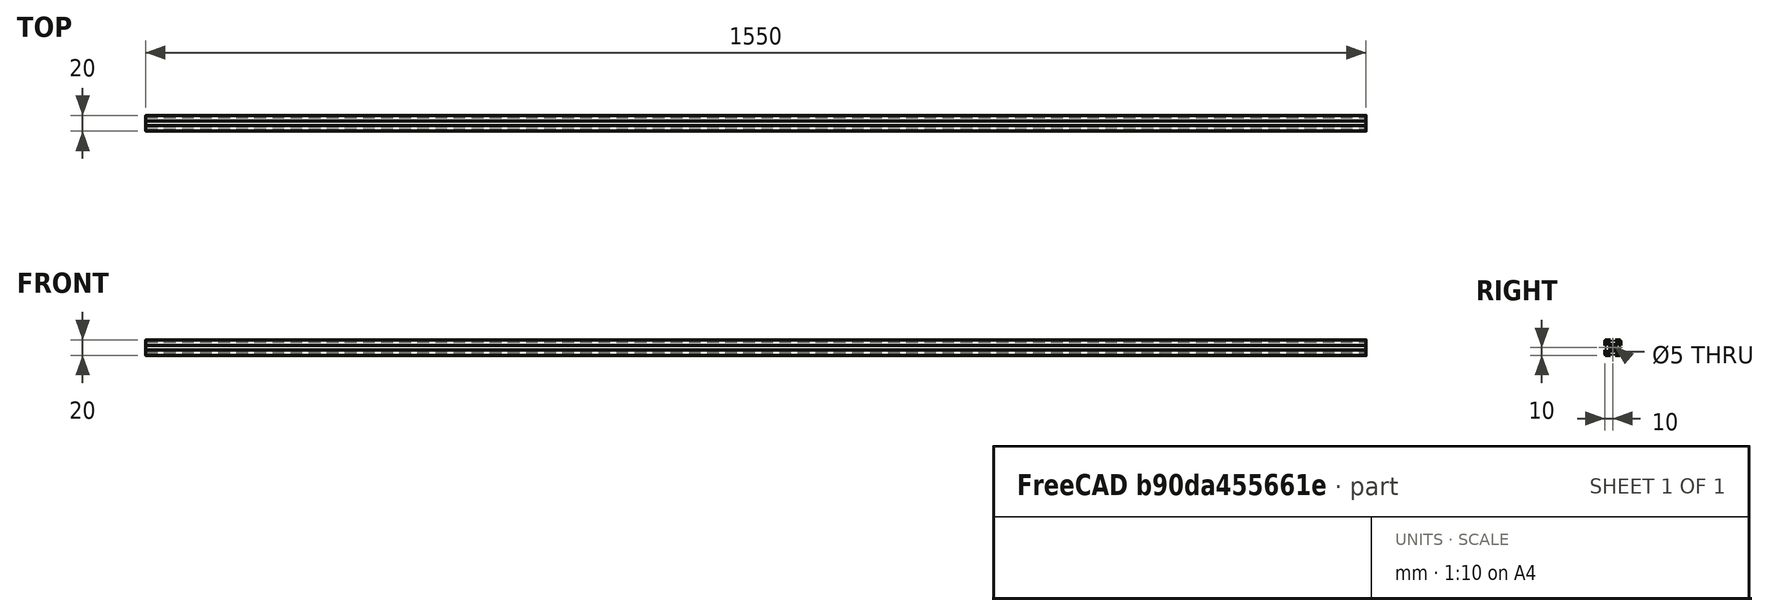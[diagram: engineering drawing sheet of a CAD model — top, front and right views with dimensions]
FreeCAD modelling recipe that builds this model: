
FCSTD DOCUMENT  (FreeCAD 0.19R24267 +99 (Git))
Label: 2020 Rail strut main long section 1550mm
License: All rights reserved
LicenseURL: http://en.wikipedia.org/wiki/All_rights_reserved
objects: Sketcher::SketchObject×1, PartDesign::Pad×1, PartDesign::Body×1
note: 4 computed .brp shape members not serialized (recipe doc carries the construction recipe); baked Part::Feature solids carry a one-line shape summary decoded from their .brp

FEATURE [Sketcher::SketchObject] Sketch  label="Rail cross section"
  FullyConstrained = true
  MapMode = 5
  Placement = pos=(0,0,0) rot=(0.57735,0.57735,0.57735;2.0944rad)
  Support = -> [YZ_Plane]
  sketch-geometry (47):
    g0: ArcOfCircle CenterX=-8 CenterY=8 CenterZ=0 NormalX=0 NormalY=0 NormalZ=1 AngleXU=0 Radius=2 StartAngle=1.5708 EndAngle=3.14159
    g1: ArcOfCircle CenterX=-8 CenterY=-8 CenterZ=0 NormalX=0 NormalY=0 NormalZ=1 AngleXU=0 Radius=2 StartAngle=3.14159 EndAngle=4.71239
    g2: ArcOfCircle CenterX=8 CenterY=-8 CenterZ=0 NormalX=0 NormalY=0 NormalZ=1 AngleXU=0 Radius=2 StartAngle=4.71239 EndAngle=6.28319
    g3: ArcOfCircle CenterX=8 CenterY=8 CenterZ=0 NormalX=0 NormalY=0 NormalZ=1 AngleXU=0 Radius=2 StartAngle=1e-16 EndAngle=1.5708
    g4: Circle CenterX=0 CenterY=0 CenterZ=0 NormalX=0 NormalY=0 NormalZ=1 AngleXU=0 Radius=2.5
    g5: LineSegment StartX=-10 StartY=8 StartZ=0 EndX=-10 EndY=3 EndZ=0
    g6: LineSegment StartX=-10 StartY=-3 StartZ=0 EndX=-10 EndY=-8 EndZ=0
    g7: LineSegment StartX=-8 StartY=-10 StartZ=0 EndX=-3 EndY=-10 EndZ=0
    g8: LineSegment StartX=3 StartY=-10 StartZ=0 EndX=8 EndY=-10 EndZ=0
    g9: LineSegment StartX=10 StartY=-8 StartZ=0 EndX=10 EndY=-3 EndZ=0
    g10: LineSegment StartX=10 StartY=3 StartZ=0 EndX=10 EndY=8 EndZ=0
    g11: LineSegment StartX=-8 StartY=10 StartZ=0 EndX=-3 EndY=10 EndZ=0
    g12: LineSegment StartX=3 StartY=10 StartZ=0 EndX=8 EndY=10 EndZ=0
    g13: LineSegment StartX=-3 StartY=4 StartZ=0 EndX=3 EndY=4 EndZ=0
    g14: LineSegment StartX=4 StartY=3 StartZ=0 EndX=4 EndY=-3 EndZ=0
    g15: LineSegment StartX=3 StartY=-4 StartZ=0 EndX=-3 EndY=-4 EndZ=0
    g16: LineSegment StartX=-4 StartY=-3 StartZ=0 EndX=-4 EndY=3 EndZ=0
    g17: LineSegment StartX=-3 StartY=-4 StartZ=0 EndX=-7 EndY=-8 EndZ=0
    g18: LineSegment StartX=-3 StartY=-10 StartZ=0 EndX=-3 EndY=-8 EndZ=0
    g19: LineSegment StartX=3 StartY=-4 StartZ=0 EndX=7 EndY=-8 EndZ=0
    g20: LineSegment StartX=4 StartY=-3 StartZ=0 EndX=8 EndY=-7 EndZ=0
    g21: LineSegment StartX=8 StartY=-7 StartZ=0 EndX=8 EndY=-3 EndZ=0
    g22: LineSegment StartX=10 StartY=-3 StartZ=0 EndX=8 EndY=-3 EndZ=0
    g23: LineSegment StartX=4 StartY=3 StartZ=0 EndX=8 EndY=7 EndZ=0
    g24: LineSegment StartX=8 StartY=7 StartZ=0 EndX=8 EndY=3 EndZ=0
    g25: LineSegment StartX=8 StartY=3 StartZ=0 EndX=10 EndY=3 EndZ=0
    g26: LineSegment StartX=3 StartY=10 StartZ=0 EndX=3 EndY=8 EndZ=0
    g27: LineSegment StartX=3 StartY=8 StartZ=0 EndX=7 EndY=8 EndZ=0
    g28: LineSegment StartX=7 StartY=8 StartZ=0 EndX=3 EndY=4 EndZ=0
    g29: LineSegment StartX=-3 StartY=4 StartZ=0 EndX=-7 EndY=8 EndZ=0
    g30: LineSegment StartX=-7 StartY=8 StartZ=0 EndX=-3 EndY=8 EndZ=0
    g31: LineSegment StartX=-3 StartY=8 StartZ=0 EndX=-3 EndY=10 EndZ=0
    g32: LineSegment StartX=-4 StartY=3 StartZ=0 EndX=-8 EndY=7 EndZ=0
    g33: LineSegment StartX=-8 StartY=3 StartZ=0 EndX=-10 EndY=3 EndZ=0
    g34: LineSegment StartX=-10 StartY=-3 StartZ=0 EndX=-8 EndY=-3 EndZ=0
    g35: LineSegment StartX=-8 StartY=-7 StartZ=0 EndX=-4 EndY=-3 EndZ=0
    g36: LineSegment StartX=3 StartY=-10 StartZ=0 EndX=3 EndY=-8 EndZ=0
    g37: LineSegment StartX=3 StartY=-8 StartZ=0 EndX=7 EndY=-8 EndZ=0
    g38: LineSegment StartX=-3 StartY=-8 StartZ=0 EndX=-7 EndY=-8 EndZ=0
    g39: LineSegment StartX=-8 StartY=-7 StartZ=0 EndX=-8 EndY=-3 EndZ=0
    g40: LineSegment StartX=-8 StartY=3 StartZ=0 EndX=-8 EndY=7 EndZ=0
    g41: LineSegment StartX=-3 StartY=10 StartZ=0 EndX=3 EndY=10 EndZ=0
    g42: LineSegment StartX=10 StartY=3 StartZ=0 EndX=10 EndY=-3 EndZ=0
    g43: LineSegment StartX=3 StartY=-10 StartZ=0 EndX=-3 EndY=-10 EndZ=0
    g44: LineSegment StartX=-10 StartY=-3 StartZ=0 EndX=-10 EndY=3 EndZ=0
    g45: LineSegment StartX=-4 StartY=-3 StartZ=0 EndX=-3 EndY=-4 EndZ=0
    g46: LineSegment StartX=-8 StartY=-7 StartZ=0 EndX=-7 EndY=-8 EndZ=0
  constraints (128):
    c: Radius(g0) = 2  'ASSUMED EDGE RADIUS'
    c: Equal(g1,g2)
    c: Coincident(g4,g-1)
    c: Radius(g4) = 2.5  'CENTER HOLE'
    c: Vertical(g6)
    c: Horizontal(g7)
    c: Horizontal(g8)
    c: Vertical(g9)
    c: Vertical(g10)
    c: Horizontal(g11)
    c: Horizontal(g12)
    c: DistanceX(g0,g3) = 20  'RAIL WIDTH'
    c: Vertical(g5)
    c: DistanceY(g2,g3) = 20  'RAIL HEIGHT'
    c: DistanceX(g7,g8) = 6  'SLOT WIDTH'
    c: Equal(g8,g7)
    c: Equal(g7,g6)
    c: Equal(g5,g11)
    c: Equal(g12,g10)
    c: Tangent(g12,g3) = 1.5708
    c: Tangent(g10,g3) = -1.5708
    c: Tangent(g11,g0) = 1.5708
    c: Tangent(g5,g0) = -1.5708
    c: Tangent(g6,g1) = -1.5708
    c: Tangent(g7,g1) = -1.5708
    c: Tangent(g8,g2) = -1.5708
    c: Tangent(g9,g2) = -1.5708
    c: Symmetric(g3,g2,g-1)
    c: Symmetric(g0,g3,g-2)
    c: Horizontal(g13)
    c: Vertical(g14)
    c: Vertical(g16)
    c: Horizontal(g15)
    c: Equal(g16,g15)
    c: Equal(g15,g14)
    c: Coincident(g17,g15)
    c: Coincident(g18,g7)
    c: Vertical(g18)
    c: Coincident(g19,g15)
    c: Coincident(g20,g14)
    c: Coincident(g21,g20)
    c: Vertical(g21)
    c: Coincident(g22,g9)
    c: Coincident(g22,g21)
    c: Coincident(g23,g14)
    c: Coincident(g24,g23)
    c: Vertical(g24)
    c: Coincident(g25,g24)
    c: Coincident(g25,g10)
    c: Coincident(g26,g12)
    c: Vertical(g26)
    c: Coincident(g27,g26)
    c: Horizontal(g27)
    c: Coincident(g28,g27)
    c: Coincident(g28,g13)
    c: Coincident(g29,g13)
    c: Coincident(g30,g29)
    c: Horizontal(g30)
    c: Coincident(g31,g30)
    c: Coincident(g31,g11)
    c: Coincident(g32,g16)
    c: Coincident(g33,g5)
    c: Horizontal(g33)
    c: Coincident(g34,g6)
    c: Horizontal(g34)
    c: Coincident(g35,g16)
    c: Coincident(g36,g8)
    c: Vertical(g36)
    c: Coincident(g37,g36)
    c: Coincident(g37,g19)
    c: Coincident(g38,g18)
    c: Coincident(g38,g17)
    c: Horizontal(g38)
    c: Coincident(g39,g35)
    c: Coincident(g39,g34)
    c: Vertical(g39)
    c: Coincident(g40,g33)
    c: Coincident(g40,g32)
    c: Vertical(g40)
    c: Horizontal(g37)
    c: Horizontal(g25)
    c: Horizontal(g22)
    c: Equal(g38,g37)
    c: Equal(g37,g21)
    c: Equal(g21,g24)
    c: Equal(g24,g27)
    c: Equal(g27,g30)
    c: Equal(g30,g40)
    c: Equal(g40,g39)
    c: Vertical(g31)
    c: Equal(g31,g26)
    c: Equal(g26,g25)
    c: Equal(g25,g22)
    c: Equal(g22,g36)
    c: Equal(g36,g18)
    c: Equal(g18,g34)
    c: Equal(g34,g33)
    c: Equal(g32,g29)
    c: Equal(g29,g28)
    c: Equal(g28,g23)
    c: Equal(g23,g20)
    c: Equal(g20,g19)
    c: Equal(g19,g17)
    c: Equal(g17,g35)
    c: Coincident(g41,g11)
    c: Coincident(g41,g12)
    c: Coincident(g42,g10)
    c: Coincident(g42,g9)
    c: Coincident(g43,g8)
    c: Coincident(g43,g7)
    c: Horizontal(g43)
    c: Coincident(g44,g6)
    c: Coincident(g44,g5)
    c: Vertical(g44)
    c: Horizontal(g41)
    c: DistanceY(g8,g15) = 6  'ASSUMED SLOT DEPTH'
    c: Equal(g43,g15)
    c: Equal(g16,g13)
    c: Equal(g44,g43)
    c: Equal(g43,g42)
    c: Equal(g42,g41)
    c: Vertical(g42)
    c: DistanceY(g36,g36) = 2  'ASSUMED WALL THICKNESS'
    c: Coincident(g45,g16)
    c: Coincident(g45,g15)
    c: Coincident(g46,g35)
    c: Coincident(g46,g17)
    c: Equal(g45,g46)
FEATURE [PartDesign::Pad] Pad  label="Length"
  Direction = (1,1,1)
  Length = 1550
  Length2 = 100
  Placement = pos=(0,0,0) rot=(0.57735,0.57735,0.57735;2.0944rad)
  Profile = -> Sketch
  Type = 0
FEATURE [PartDesign::Body] Body
  Group = -> [Sketch,Pad]
  Origin = -> Origin
  Tip = -> Pad
